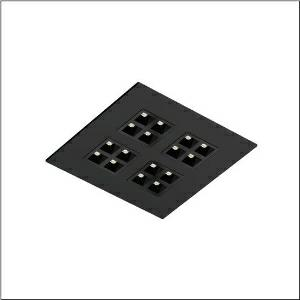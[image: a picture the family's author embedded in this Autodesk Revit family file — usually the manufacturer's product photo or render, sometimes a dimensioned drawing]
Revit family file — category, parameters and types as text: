
# Revit family: silica_31_square_51my6lds34ba
name_source: partatom
category: Lighting Fixtures
units: mm (PartAtom-declared; Revit-internal decimal feet)

## family parameters
Cut with Voids When Loaded = No
Host = Face
Light Source = No
Part Type = Normal
Room Calculation Point = No
Round Connector Dimension = Use Diameter
Shared = No

## types (1)
- --- (1 x LED, 5980 lm, 38.5 W, 3000K)
    Apparent Load = 39 VA
    CIE Flux Codes = 82 100 100 100 100
    Color Rendering = 80
    Color Temperature = 3000K
    Default Elevation = 1800 mm
    Description = Silica 31 Square, office luminaire, primary light control with lens, of PMMA, primary anti-glare with reflector, of PC, black, light emission: direct distribution, primary light characteristic: symmetric, installation type: lay-in mounting, LED, rated luminous flux: 4.650lm, luminous efficacy: 158lm/W, light colour: 830, colour temperature: 3000K, control gear: DALI 2, Multilumen, with terminal, 5-pole, mains connection: 220..240V, AC, 50/60Hz, rated input power: 29.4W, luminaire housing, of sheet steel, coated, jet black (RAL 9005), module: M600, length: 595mm, width: 595mm, height: 43mm, protection rating (complete): IP20, insulation class (complete): insulation class II (safety insulation), certification: CE, impact resistance: IK03, permissible operating ambient temperature: -20..+35°C, standard: EN 50419, packaging unit: 1 piece
    Height = 0 mm  [stored 0 ft]
    Lamp = 1 x LED
    Lamp Light Flux = 5980 lm
    Lamp Power = 38.5 W
    Lamp count = 1
    Length = 595 mm
    Luminous efficacy = 155 lm/W
    Manufacturer = Siteco
    ModVariant = No
    Model = 51MY6LDS34BA
    Mounting Place = Ceiling
    Mounting Type = Recessed
    Number of Poles = 1
    OnlyDefault = Yes
    Power Factor = 1
    Product Name = Silica 31 Square
    Product group = office luminaire | ceiling recessed
    ProductGroupID = 400
    Protection Class = Protection class II
    Protection Degree = IP 20
    RLX_Detail_Level = 1
    RLX_Emergency_Light_Flux = 0 lm
    RLX_Emergency_Type = 0
    RLX_Emergency_Type_DB = No
    RlxData = <blob elided: 35361 chars, md5=d25d0d92>
    Socket = socket
    Standby Power = 0 W
    System Light Flux = 5980 lm
    System Power = 39 W
    Type Comments = factory setting: luminous flux: 100 % | (OFF | OFF | OFF | OFF) | 1050 mA
    Type Image = l_1313660.jpg
    URL = http://relux.com
    VarID = @adj_043183
    Voltage = 0 V
    Weight = 0.00 kg
    Width = 595 mm

note: [stored X ft] marks values corroborated as IEEE doubles in the binary element streams (Revit-internal decimal feet)

## geometry (parser evidence)
native form markers: Blend x4, Sweep x9
no freeform markers — native parametric forms only
